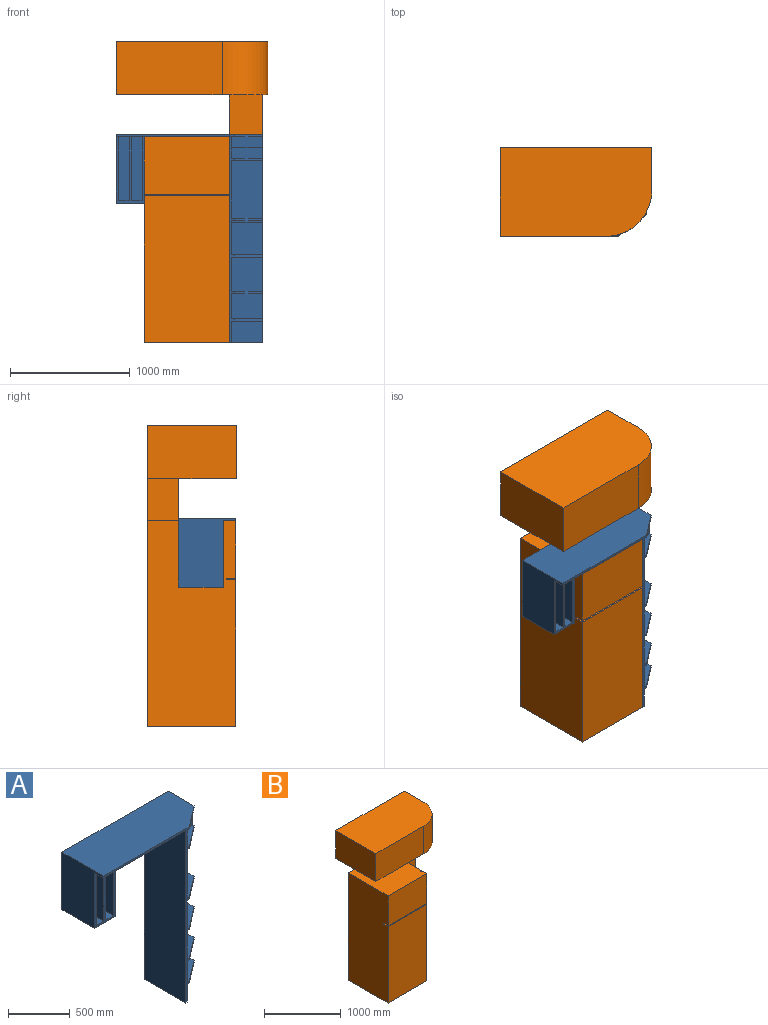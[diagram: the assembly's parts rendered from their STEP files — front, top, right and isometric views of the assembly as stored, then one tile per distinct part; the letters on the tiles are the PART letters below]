
ASSEMBLY  parts=2 mates=1
PART A: 87 faces, bbox 1219.2x476.3x1733.6 mm
  f0: plane 257.18x69.85mm, normal (0,0,1), area 17963.7mm2, adj f1,f24,f70,f74
  f1: plane 457.2x177.8mm, normal (1,0,0), area 76209.5mm2, adj f0,f2,f3,f4,f20,f21,f63,f66
  f2: plane 257.18x69.85mm, normal (0,0,1), area 17963.7mm2, adj f1,f24,f67,f71
  f3: plane 257.18x69.85mm, normal (0,0,1), area 17963.7mm2, adj f1,f4,f24,f68
  f4: plane 257.18x177.8mm, normal (0,-1,0), area 45725.7mm2, adj f1,f3,f24,f63
  f5: plane 482.6x457.2mm, normal (1,0,0), area 220644.7mm2, adj f11,f20,f35,f65
  f6: plane 257.18x25.4mm, normal (0,0,-1), area 6532.2mm2, adj f8,f12,f24,f54
  f7: plane 257.18x76.2mm, normal (0,0,-1), area 19596.7mm2, adj f8,f24,f50,f55
  f8: plane 457.2x285.75mm, normal (1,0,0), area 128951.4mm2, adj f6,f7,f9,f10,f12,f20,f32,f36
  f9: plane 257.18x76.2mm, normal (0,0,-1), area 19596.7mm2, adj f8,f24,f40,f46
  f10: plane 257.18x25.4mm, normal (0,0,-1), area 6532.2mm2, adj f8,f24,f38,f51
  f11: plane 482.6x257.18mm, normal (0,-1,0), area 124112.7mm2, adj f5,f24,f35,f65
  f12: plane 285.75x257.18mm, normal (0,-1,0), area 73487.8mm2, adj f6,f8,f24,f32
  f13: plane 457.2x285.75mm, normal (1,0,0), area 130644.9mm2, adj f14,f20,f29,f33
  f14: plane 285.75x257.18mm, normal (0,-1,0), area 73487.8mm2, adj f13,f24,f29,f33
  f15: plane 457.2x209.55mm, normal (1,0,0), area 95806.3mm2, adj f17,f20,f26,f30
  f16: plane 457.2x177.8mm, normal (1,0,0), area 81290.2mm2, adj f20,f22,f23,f27
  f17: plane 257.18x209.55mm, normal (0,-1,0), area 53891mm2, adj f15,f24,f26,f30
  f18: plane 1733.55x1219.2mm, normal (0,1,0), area 626611.6mm2, adj f19,f22,f24,f57,f61,f62,f76,f85
  f19: plane 1714.5x476.25mm, normal (-1,0,0), area 816530.6mm2, adj f18,f20,f21,f22,f57
  f20: plane 1714.5x44.45mm, normal (0,-1,0), area 35080.6mm2, adj f1,f5,f8,f13,f15,f16,f19,f21
  f21: plane 19.05x1.25mm, normal (0,0,1), area 18.7mm2, adj f1,f19,f20,f59
  f22: plane 476.25x276.23mm, normal (0,0,-1), area 13971.7mm2, adj f16,f18,f19,f20,f23,f24
  f23: plane 257.18x177.8mm, normal (0,-1,0), area 45725.7mm2, adj f16,f22,f24,f27
  f24: plane 1733.55x298.45mm, normal (1,0,0), area 71733.7mm2, adj f0,f2,f3,f4,f6,f7,f9,f10
  f25: plane 231.78x177.8mm, normal (0.61,-0.79,0), area 5564.8mm2, adj f20,f24,f26,f27
  f26: plane 457.2x257.18mm, normal (0,0,1), area 96975.6mm2, adj f15,f17,f20,f24,f25
  f27: plane 457.2x257.18mm, normal (0,0,-1), area 96975.6mm2, adj f16,f20,f23,f24,f25
  f28: plane 231.78x177.8mm, normal (0.61,-0.79,0), area 5564.8mm2, adj f20,f24,f29,f30
  f29: plane 457.2x257.18mm, normal (0,0,1), area 96975.6mm2, adj f13,f14,f20,f24,f28
  f30: plane 457.2x257.18mm, normal (0,0,-1), area 96975.6mm2, adj f15,f17,f20,f24,f28
  f31: plane 231.78x177.8mm, normal (0.61,-0.79,0), area 5564.8mm2, adj f20,f24,f32,f33
  f32: plane 457.2x257.18mm, normal (0,0,1), area 96975.6mm2, adj f8,f12,f20,f24,f31
  f33: plane 457.2x257.18mm, normal (0,0,-1), area 96975.6mm2, adj f13,f14,f20,f24,f31
  f34: plane 231.78x177.8mm, normal (0.61,-0.79,0), area 5564.8mm2, adj f20,f24,f35,f36
  f35: plane 457.2x257.18mm, normal (0,0,1), area 96975.6mm2, adj f5,f11,f20,f24,f34
  f36: plane 257.18x203.2mm, normal (0,0,-1), area 31653.2mm2, adj f8,f20,f24,f34,f42
  f37: plane 257.18x28.58mm, normal (0,0,-1), area 7348.8mm2, adj f8,f24,f38,f39
  f38: plane 257.18x19.05mm, normal (0,1,0), area 4899.2mm2, adj f8,f10,f24,f37
  f39: plane 257.18x11.43mm, normal (0,-1,0), area 2939.5mm2, adj f8,f24,f37,f41
  f40: plane 257.18x7.62mm, normal (0,-1,0), area 1959.7mm2, adj f8,f9,f24,f41
  f41: plane 257.18x15.88mm, normal (0,0,1), area 4082.7mm2, adj f8,f24,f39,f40
  f42: plane 257.18x19.05mm, normal (0,-1,0), area 4899.2mm2, adj f8,f24,f36,f43
  f43: plane 257.18x28.58mm, normal (0,0,-1), area 7348.8mm2, adj f8,f24,f42,f44
  f44: plane 257.18x11.43mm, normal (0,1,0), area 2939.5mm2, adj f8,f24,f43,f45
  f45: plane 257.18x15.88mm, normal (0,0,1), area 4082.7mm2, adj f8,f24,f44,f46
  f46: plane 257.18x7.62mm, normal (0,1,0), area 1959.7mm2, adj f8,f9,f24,f45
  f47: plane 257.18x28.58mm, normal (0,0,-1), area 7348.8mm2, adj f8,f24,f48,f51
  f48: plane 257.18x11.43mm, normal (0,1,0), area 2939.5mm2, adj f8,f24,f47,f49
  f49: plane 257.18x15.88mm, normal (0,0,1), area 4082.7mm2, adj f8,f24,f48,f50
  f50: plane 257.18x7.62mm, normal (0,1,0), area 1959.7mm2, adj f7,f8,f24,f49
  f51: plane 257.18x19.05mm, normal (0,-1,0), area 4899.2mm2, adj f8,f10,f24,f47
  f52: plane 257.18x11.43mm, normal (0,-1,0), area 2939.5mm2, adj f8,f24,f53,f56
  f53: plane 257.18x28.58mm, normal (0,0,-1), area 7348.8mm2, adj f8,f24,f52,f54
  f54: plane 257.18x19.05mm, normal (0,1,0), area 4899.2mm2, adj f6,f8,f24,f53
  f55: plane 257.18x7.62mm, normal (0,-1,0), area 1959.7mm2, adj f7,f8,f24,f56
  f56: plane 257.18x15.88mm, normal (0,0,1), area 4082.7mm2, adj f8,f24,f52,f55
  f57: plane 942.98x475mm, normal (0,0,-1), area 423118.4mm2, adj f18,f19,f58,f61,f76,f77,f78,f79
  f58: plane 942.98x19.05mm, normal (0,-1,0), area 17963.7mm2, adj f57,f59,f61,f62
  f59: plane 44.45x19.05mm, normal (-0.03,-1,0), area 847.1mm2, adj f21,f58,f60,f62,f63
  f60: plane 231.78x177.8mm, normal (0.61,-0.79,0), area 5564.8mm2, adj f24,f59,f62,f63
  f61: plane 571.5x475mm, normal (-1,0,0), area 216024.2mm2, adj f18,f57,f58,f62,f77,f85
  f62: plane 1219.2x476.25mm, normal (0,0,1), area 558836.3mm2, adj f18,f24,f58,f59,f60,f61
  f63: plane 457.2x257.18mm, normal (0,0,-1), area 96966.6mm2, adj f1,f4,f24,f59,f60
  f64: plane 231.78x177.8mm, normal (0.61,-0.79,0), area 5564.8mm2, adj f20,f24,f65,f66
  f65: plane 457.2x257.18mm, normal (0,0,-1), area 96975.6mm2, adj f5,f11,f20,f24,f64
  f66: plane 257.18x190.5mm, normal (0,0,1), area 28387mm2, adj f1,f20,f24,f64,f73
  f67: plane 257.18x88.9mm, normal (0,-1,0), area 22862.9mm2, adj f1,f2,f24,f69
  f68: plane 257.18x88.9mm, normal (0,1,0), area 22862.9mm2, adj f1,f3,f24,f69
  f69: plane 257.18x19.05mm, normal (0,0,1), area 4899.2mm2, adj f1,f24,f67,f68
  f70: plane 257.18x88.9mm, normal (0,-1,0), area 22862.9mm2, adj f0,f1,f24,f72
  f71: plane 257.18x88.9mm, normal (0,1,0), area 22862.9mm2, adj f1,f2,f24,f72
  f72: plane 257.18x19.05mm, normal (0,0,1), area 4899.2mm2, adj f1,f24,f70,f71
  f73: plane 257.18x88.9mm, normal (0,-1,0), area 22862.9mm2, adj f1,f24,f66,f75
  f74: plane 257.18x88.9mm, normal (0,1,0), area 22862.9mm2, adj f0,f1,f24,f75
  f75: plane 257.18x19.05mm, normal (0,0,1), area 4899.2mm2, adj f1,f24,f73,f74
  f76: plane 552.45x374.65mm, normal (1,0,0), area 206975.4mm2, adj f18,f57,f77,f85
  f77: plane 552.45x234.95mm, normal (0,-1,0), area 34959.6mm2, adj f57,f61,f76,f78,f80,f81,f83,f84
  f78: plane 533.4x355.6mm, normal (-1,0,0), area 189677mm2, adj f57,f77,f79,f84
  f79: plane 533.4x88.9mm, normal (0,-1,0), area 47419.3mm2, adj f57,f78,f80,f84
  f80: plane 533.4x355.6mm, normal (1,0,0), area 189677mm2, adj f57,f77,f79,f84
  f81: plane 533.4x355.6mm, normal (-1,0,0), area 189677mm2, adj f57,f77,f82,f86
  f82: plane 533.4x88.9mm, normal (0,-1,0), area 47419.3mm2, adj f57,f81,f83,f86
  f83: plane 533.4x355.6mm, normal (1,0,0), area 189677mm2, adj f57,f77,f82,f86
  f84: plane 355.6x88.9mm, normal (0,0,1), area 31612.8mm2, adj f77,f78,f79,f80
  f85: plane 374.65x234.95mm, normal (0,0,-1), area 88024mm2, adj f18,f61,f76,f77
  f86: plane 355.6x88.9mm, normal (0,0,1), area 31612.8mm2, adj f77,f81,f82,f83
PART B: 25 faces, bbox 1263.7x739.8x2508.3 mm
  f0: plane 479.43x76.2mm, normal (1,0,0), area 36532.2mm2, adj f2,f3,f12,f15
  f1: plane 1714.5x381mm, normal (1,0,0), area 653224.5mm2, adj f2,f6,f9,f17
  f2: plane 733.43x711.2mm, normal (0,0,1), area 521128mm2, adj f0,f1,f3,f5,f8,f10,f15,f17
  f3: plane 711.2x479.43mm, normal (0,-1,0), area 340967.1mm2, adj f0,f2,f10,f12
  f4: plane 1222.38x76.2mm, normal (1,0,0), area 93145mm2, adj f9,f11,f13,f16
  f5: plane 349.25x257.18mm, normal (-1,0,0), area 89818.4mm2, adj f2,f6,f8,f24
  f6: plane 2063.75x276.23mm, normal (0,-1,0), area 570059.3mm2, adj f1,f5,f7,f9,f24
  f7: plane 2063.75x257.18mm, normal (1,0,0), area 530744.9mm2, adj f6,f8,f9,f24
  f8: plane 2508.25x1263.65mm, normal (0,1,0), area 2351104.2mm2, adj f2,f5,f7,f9,f10,f19,f20,f23
  f9: plane 987.43x733.43mm, normal (0,0,-1), area 592166.2mm2, adj f1,f4,f6,f7,f8,f10,f11,f16
  f10: plane 1714.5x733.43mm, normal (-1,0,0), area 1256489.4mm2, adj f2,f3,f8,f9,f11,f12,f13,f14
  f11: plane 1222.38x711.2mm, normal (0,-1,0), area 869353.1mm2, adj f4,f9,f10,f13
  f12: plane 711.2x76.2mm, normal (0,0,-1), area 54193.4mm2, adj f0,f3,f10,f14,f15
  f13: plane 711.2x76.2mm, normal (0,0,1), area 54193.4mm2, adj f4,f10,f11,f14,f16
  f14: plane 685.8x12.7mm, normal (0,-1,0), area 8709.7mm2, adj f10,f12,f13,f18
  f15: plane 479.43x25.4mm, normal (0,1,0), area 12177.4mm2, adj f0,f2,f12,f18
  f16: plane 1222.38x25.4mm, normal (0,1,0), area 31048.3mm2, adj f4,f9,f13,f18
  f17: plane 1714.5x25.4mm, normal (0,-1,0), area 43548.3mm2, adj f1,f2,f9,f18
  f18: plane 1714.5x19.05mm, normal (1,0,0), area 32661.2mm2, adj f2,f9,f14,f15,f16,f17
  f19: plane 444.5x358.78mm, normal (1,0,0), area 159475.5mm2, adj f8,f22,f23,f24
  f20: plane 739.78x444.5mm, normal (-1,0,0), area 328830mm2, adj f8,f21,f23,f24
  f21: plane 882.65x444.5mm, normal (0,-1,0), area 392337.9mm2, adj f20,f22,f23,f24
  f22: cylinder r=381mm len=444.5mm, axis (0,0,-1), area 266021.4mm2, adj f19,f21,f23,f24
  f23: plane 1263.65x739.78mm, normal (0,0,1), area 903664.9mm2, adj f8,f19,f20,f21,f22
  f24: plane 1263.65x739.78mm, normal (0,0,-1), area 832626.7mm2, adj f5,f6,f7,f8,f19,f20,f21,f22
PLACE A t=(-2073.02,-397.03,-554.51)mm
PLACE B t=(-2073.02,-397.03,-554.51)mm fixed
MATE fastened A.f24 <-> B.f7  axis (1,0,0) through (-1796.8,-397.03,-554.51)mm
